# Revit family: FU_Table_LAPSE 0440MA
name_source: partatom
category: Furniture
units: mm (PartAtom-declared; Revit-internal decimal feet)

## family parameters
Always vertical = Yes
Cut with Voids When Loaded = No
OmniClass Number = 23.40.20.00
OmniClass Title = General Furniture and Specialties
Room Calculation Point = No
Shared = No
Work Plane-Based = No

## types (1)
- LAPSE 0440MA
    Default Elevation = 0 mm  [stored 0 ft]
    Depth = 720 mm  [stored 2.3622 ft]
    Description = Table top in Oak veneer or lacquered MDF. Optional USB charging devices, wireless charging devices or double outlet extensions can be fitted to the unit.
    Elevation = 359 mm  [stored 1.17782 ft]
    Manufacturer = Sandler
    Model = LAPSE 0440MA
    URL = https://www.sandlerseating.com
    Width = 360 mm  [stored 1.1811 ft]

note: [stored X ft] marks values corroborated as IEEE doubles in the binary element streams (Revit-internal decimal feet)

## geometry (parser evidence)
native form markers: Sweep x6
no freeform markers — native parametric forms only
